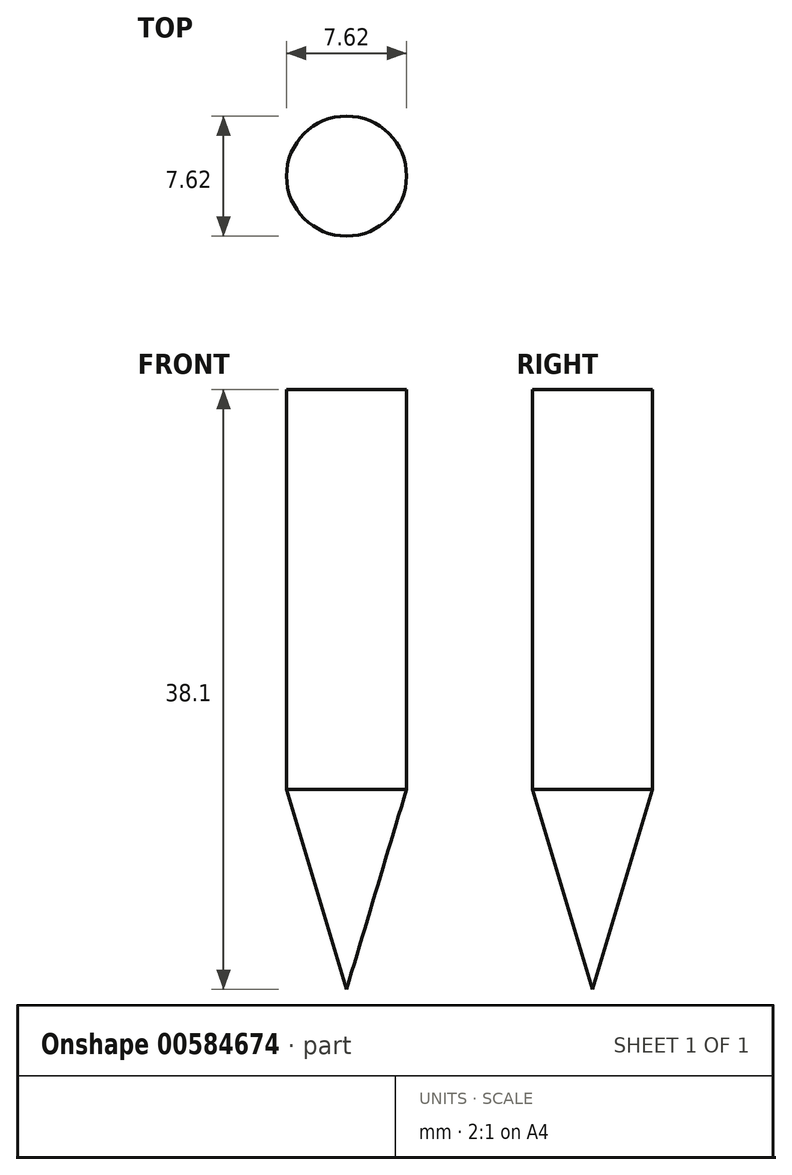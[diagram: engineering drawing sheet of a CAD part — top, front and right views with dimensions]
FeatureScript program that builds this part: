
annotation { "Feature Type Name" : "Feature", "Feature Type Description" : "" }
export const myFeature = defineFeature(function(context is Context, id is Id, definition is map)
    precondition{}
    {
        {
            var Q0;
            Q0=qCreatedBy(makeId("Front.planeOp"),FACE);
            var sketch = newSketch(context, id + "F0", { "sketchPlane" : qUnion([Q0])});
            skLineSegment(sketch, "E0", {"start": v(0, -12.7) * mm, "end": v(-3.8, 0) * mm});
            skLineSegment(sketch, "E1", {"start": v(-3.8, 0) * mm, "end": v(-3.8, 25.4) * mm});
            skLineSegment(sketch, "E2", {"start": v(-3.8, 25.4) * mm, "end": v(0, 25.4) * mm});
            skLineSegment(sketch, "E3", {"start": v(0, 25.4) * mm, "end": v(0, -12.7) * mm});
            skSolve(sketch);
        }
        {
            var Q0;
            Q0 = qSketchRegion(id + "F0", true);
            var Q1;
            Q1=sQuery(id+"F0.wireOp",EDGE,"E3");
            revolve(context, id + "F1", {"entities" : qUnion([Q0]), "axis" : qUnion([Q1]), "revolveType" : RevolveType.FULL});
        }
    });
